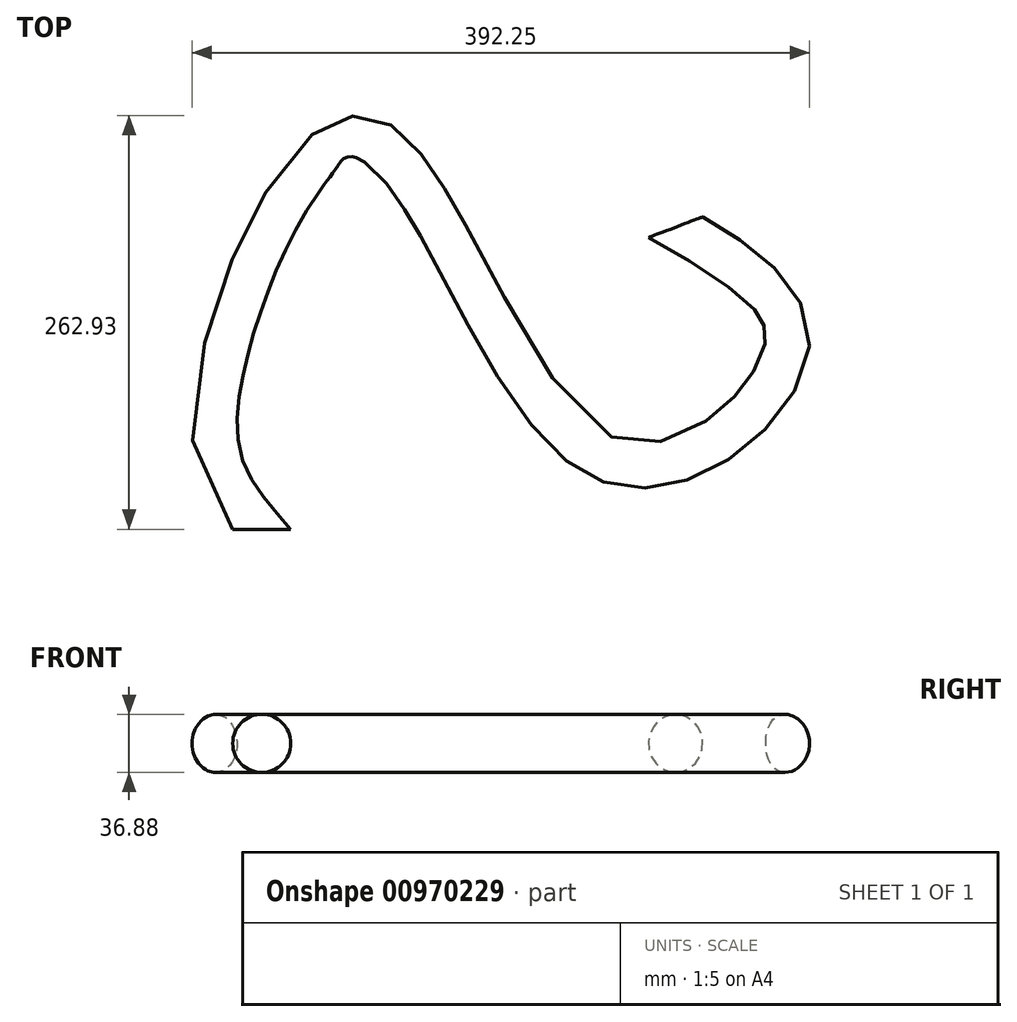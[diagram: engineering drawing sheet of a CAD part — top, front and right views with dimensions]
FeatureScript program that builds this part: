
annotation { "Feature Type Name" : "Feature", "Feature Type Description" : "" }
export const myFeature = defineFeature(function(context is Context, id is Id, definition is map)
    precondition{}
    {
        {
            var Q0;
            Q0=qCreatedBy(makeId("Top.planeOp"),FACE);
            var sketch = newSketch(context, id + "F0", { "sketchPlane" : qUnion([Q0])});
            skFitSpline(sketch, "E0", {"points": [v(0, 0) * mm, v(-27.18, 92.59) * mm, v(65.2, 246.57) * mm, v(218, 46.12) * mm, v(331.76, 113.42) * mm, v(262.86, 191.94) * mm], "startDerivative": vector(-441.33, 540.73) * mm, "endDerivative": vector(-677.3, 390.02) * mm});
            skSolve(sketch);
        }
        {
            var Q0;
            Q0=qCreatedBy(makeId("Front.planeOp"),FACE);
            var sketch = newSketch(context, id + "F1", { "sketchPlane" : qUnion([Q0])});
            skCircle(sketch, "E1", {"center": v(0, 0) * mm, "radius": 18.44 * mm});
            skSolve(sketch);
        }
        {
            var Q0;
            Q0=makeQuery(id+"F1.imprint","IMPRINT",FACE,{"disambiguationData":[TD([[makeQuery(id+"F1.imprint","IMPRINT",EDGE,{"derivedFrom":sQuery(id+"F1.wireOp",EDGE,"E1")}),1.0]])]});
            var Q1;
            Q1=sQuery(id+"F0.wireOp",EDGE,"E0");
            sweep(context, id + "F2", {"profiles" : qUnion([Q0]), "path" : qUnion([Q1])});
        }
    });
